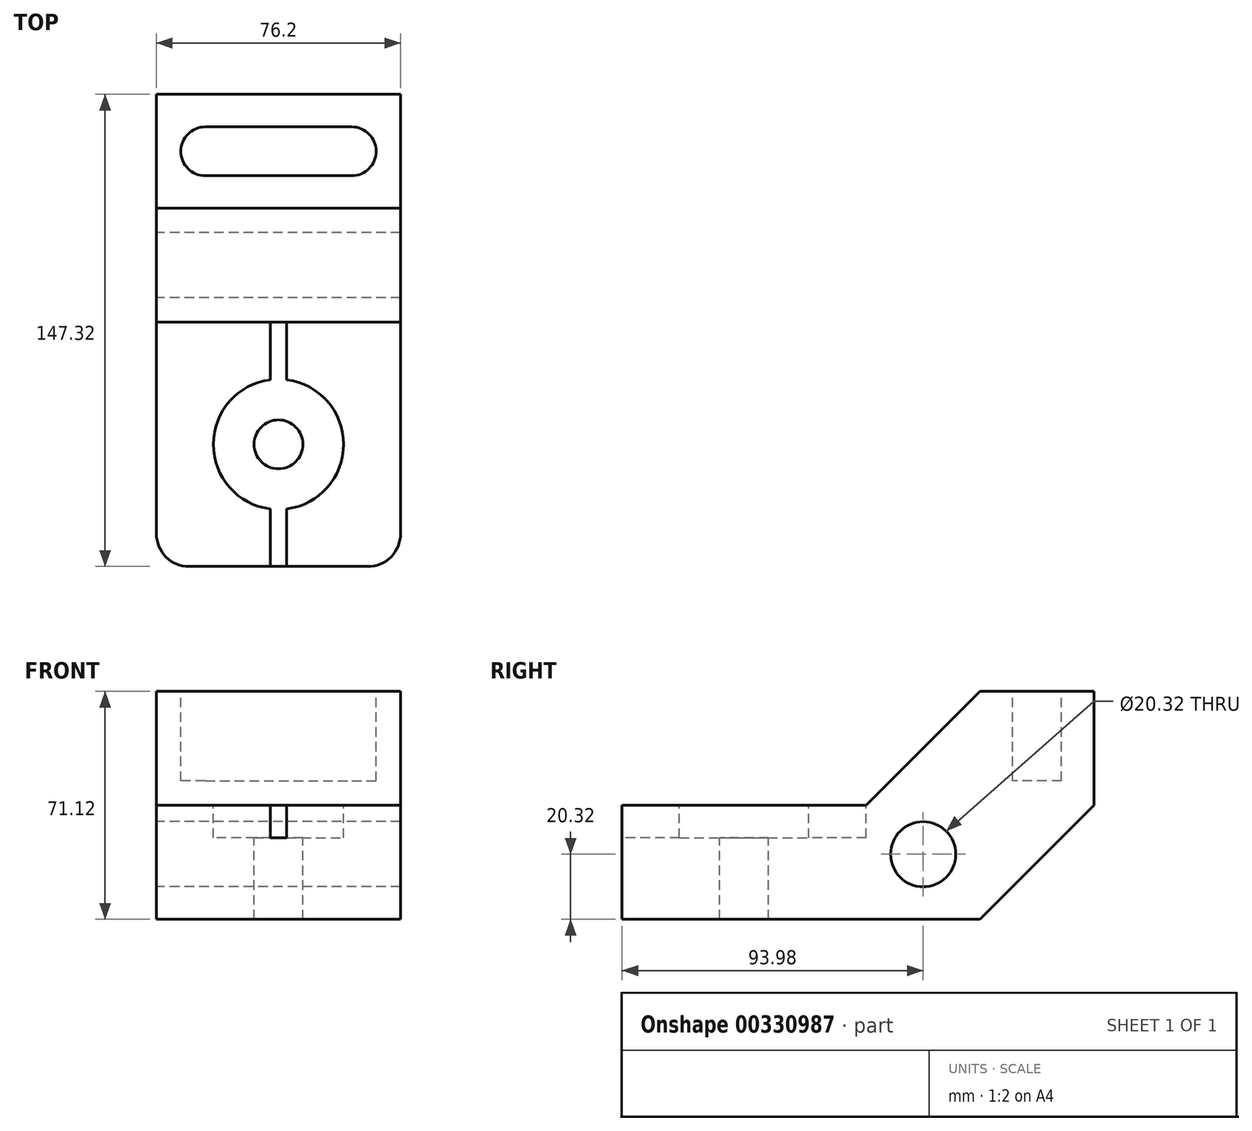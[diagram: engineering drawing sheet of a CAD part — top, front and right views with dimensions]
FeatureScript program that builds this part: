
annotation { "Feature Type Name" : "Feature", "Feature Type Description" : "" }
export const myFeature = defineFeature(function(context is Context, id is Id, definition is map)
    precondition{}
    {
        {
            var Q0;
            Q0=qCreatedBy(makeId("Right.planeOp"),FACE);
            var sketch = newSketch(context, id + "F0", { "sketchPlane" : qUnion([Q0])});
            skCircle(sketch, "E0", {"center": v(0, 0) * mm, "radius": 10.16 * mm});
            skLineSegment(sketch, "E1", {"start": v(-93.98, -20.32) * mm, "end": v(17.78, -20.32) * mm});
            skLineSegment(sketch, "E2", {"start": v(17.78, -20.32) * mm, "end": v(53.34, 15.24) * mm});
            skLineSegment(sketch, "E3", {"start": v(53.34, 15.24) * mm, "end": v(53.34, 50.8) * mm});
            skLineSegment(sketch, "E4", {"start": v(53.34, 50.8) * mm, "end": v(17.78, 50.8) * mm});
            skLineSegment(sketch, "E5", {"start": v(17.78, 50.8) * mm, "end": v(-17.78, 15.24) * mm});
            skLineSegment(sketch, "E6", {"start": v(-17.78, 15.24) * mm, "end": v(-93.98, 15.24) * mm});
            skLineSegment(sketch, "E7", {"start": v(-93.98, 15.24) * mm, "end": v(-93.98, -20.32) * mm});
            skSolve(sketch);
        }
        {
            var Q0;
            Q0 = qSketchRegion(id + "F0", true);
            extrude(context, id + "F1", {"entities" : qUnion([Q0]), "endBound" : BoundingType.SYMMETRIC, "depth" : 76.2 * mm});
        }
        {
            var Q0;
            Q0=makeQuery(id+"F1.opExtrude","SWEPT_FACE",FACE,{"disambiguationData":[OSD([sQuery(id+"F0.wireOp",EDGE,"E6")])]});
            var sketch = newSketch(context, id + "F2", { "sketchPlane" : qUnion([Q0])});
            skPoint(sketch, "E8", {"position": v(0, -55.88) * mm});
            skSolve(sketch);
        }
        {
            var Q0;
            Q0=sQuery(id+"F2.wireOp",VERTEX,"E8");
            var Q1;
            Q1=makeQuery(id+"F1.opExtrude","SWEPT_BODY",BODY,{"disambiguationData":[OSD([sQuery(id+"F0.wireOp",EDGE,"E0"),sQuery(id+"F0.wireOp",EDGE,"E1"),sQuery(id+"F0.wireOp",EDGE,"E2"),sQuery(id+"F0.wireOp",EDGE,"E3"),sQuery(id+"F0.wireOp",EDGE,"E4"),sQuery(id+"F0.wireOp",EDGE,"E5"),sQuery(id+"F0.wireOp",EDGE,"E6"),sQuery(id+"F0.wireOp",EDGE,"E7")])]});
            hole(context, id + "F3", {"style" : HoleStyle.C_BORE, "endStyle" : HoleEndStyle.THROUGH, "holeDiameter" : 15.24 * mm, "cBoreDiameter" : 40.64 * mm, "cBoreDepth" : 10.16 * mm, "tappedDepth" : 12.7 * mm, "tapClearance" : 3, "locations" : qUnion([Q0]), "scope" : qUnion([Q1])});
        }
        {
            var Q0;
            Q0=makeQuery(id+"F1.opExtrude","CAP_EDGE",EDGE,{"disambiguationData":[OSD([sQuery(id+"F0.wireOp",EDGE,"E7")])],"isStart":false});
            var Q1;
            Q1=makeQuery(id+"F1.opExtrude","CAP_EDGE",EDGE,{"disambiguationData":[OSD([sQuery(id+"F0.wireOp",EDGE,"E7")])],"isStart":true});
            fillet(context, id + "F4", {"entities" : qUnion([Q0, Q1]), "radius" : 10.16 * mm, "tangentPropagation" : true, "allowEdgeOverflow" : false});
        }
        {
            var Q0;
            Q0=makeQuery(id+"F1.opExtrude","SWEPT_FACE",FACE,{"disambiguationData":[OSD([sQuery(id+"F0.wireOp",EDGE,"E6")])]});
            var sketch = newSketch(context, id + "F5", { "sketchPlane" : qUnion([Q0])});
            skLineSegment(sketch, "E9.bottom", {"start": v(-2.54, -17.78) * mm, "end": v(2.54, -17.78) * mm});
            skLineSegment(sketch, "E9.top", {"start": v(-2.54, -93.98) * mm, "end": v(2.54, -93.98) * mm});
            skLineSegment(sketch, "E9.left", {"start": v(-2.54, -17.78) * mm, "end": v(-2.54, -93.98) * mm});
            skLineSegment(sketch, "E9.right", {"start": v(2.54, -17.78) * mm, "end": v(2.54, -93.98) * mm});
            skSolve(sketch);
        }
        {
            var Q0;
            Q0 = qSketchRegion(id + "F5", true);
            extrude(context, id + "F6", {"entities" : qUnion([Q0]), "operationType" : NewBodyOperationType.REMOVE, "oppositeDirection" : true, "depth" : 10.16 * mm});
        }
        {
            var Q0;
            Q0=makeQuery(id+"F1.opExtrude","SWEPT_FACE",FACE,{"disambiguationData":[OSD([sQuery(id+"F0.wireOp",EDGE,"E4")])]});
            var sketch = newSketch(context, id + "F7", { "sketchPlane" : qUnion([Q0])});
            skLineSegment(sketch, "E10", {"start": v(-22.86, 43.18) * mm, "end": v(22.86, 43.18) * mm});
            skLineSegment(sketch, "E11", {"start": v(22.86, 27.94) * mm, "end": v(-22.86, 27.94) * mm});
            skArc(sketch, "E12", {"start": v(-22.86, 43.18) * mm, "mid": v(-30.48, 35.56) * mm, "end": v(-22.86, 27.94) * mm});
            skArc(sketch, "E13", {"start": v(22.86, 27.94) * mm, "mid": v(30.48, 35.56) * mm, "end": v(22.86, 43.18) * mm});
            skSolve(sketch);
        }
        {
            var Q0;
            Q0 = qSketchRegion(id + "F7", true);
            extrude(context, id + "F8", {"entities" : qUnion([Q0]), "operationType" : NewBodyOperationType.REMOVE, "oppositeDirection" : true, "depth" : 27.94 * mm});
        }
    });
